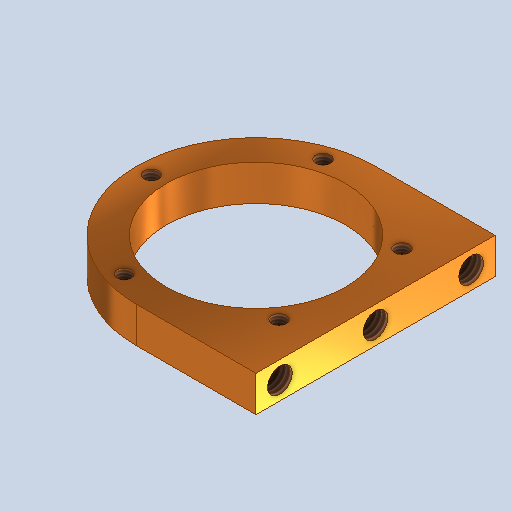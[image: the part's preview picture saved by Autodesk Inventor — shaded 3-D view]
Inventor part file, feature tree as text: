
AUTODESK INVENTOR PART (.ipt)
format: ipt  version: 2025.1 (Build 291241000, 241)  size: 299,008 bytes
history: native  units: mm
features: sketch x4, hole x3, extrude x2, pattern_circular x1
ambient origin geometry x8: Origin, YZ Plane, XZ Plane, XY Plane, X Axis, Y Axis, Z Axis, Center Point
bodies: Solid1 (feature_tree)
feature tree (10):
  extrude  "Extrusion1"  Depth=20.0mm
  hole  "Hole1"  [1 undecoded]
  pattern_circular  "Circular Pattern1"  Count=5 Angle=360.0deg
  sketch  "Sketch4"  dims[d5=35.0mm]
  hole  "Hole2"  [1 undecoded]
  hole  "Hole3"  [1 undecoded]
  extrude  "Extrusion2"  Depth=10.0mm
  sketch  "Sketch1"  dims[d0=20.0mm d1=20.0mm]
  sketch  "Sketch2"  dims[d2=6.0mm d3=0.0mm d4=20.0mm]
  sketch  "Sketch5"  dims[d6=2.459mm d7=6.0mm d8=4.0mm d9=2.0mm d10=90.0deg d11=8.0mm d12=0.0mm d13=50.0mm d14=360.0deg d16=32.0mm d17=16.0mm d18=4.134mm d19=10.0mm d20=4.0mm d21=2.0mm d22=90.0deg d23=14.2mm d24=0.0mm d25=4.134mm d26=10.0mm d27=4.0mm d28=2.0mm d29=90.0deg d30=14.2mm d31=0.0mm d32=30.0mm d33=6.0mm d34=0.0mm]
note: 3 required parameter values undecoded (feature->parameter linkage not recoverable at this tier; creation-order binding heuristic only, values carry confidence <= 0.55)
